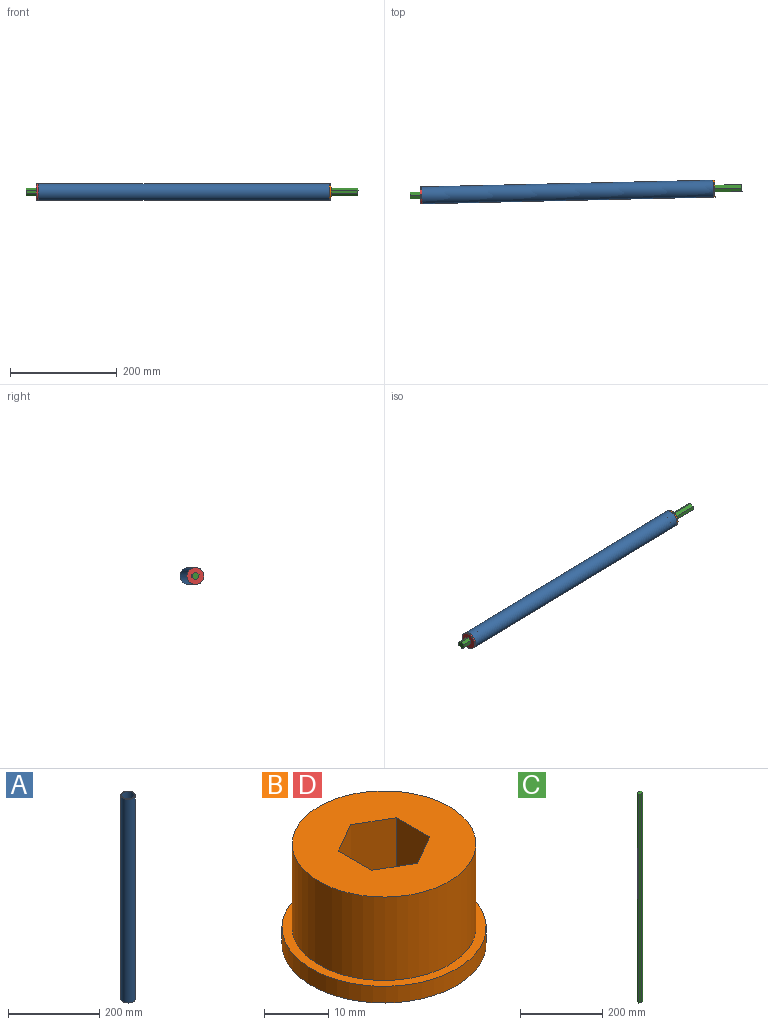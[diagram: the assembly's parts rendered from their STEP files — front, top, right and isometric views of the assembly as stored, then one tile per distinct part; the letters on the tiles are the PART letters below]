
ASSEMBLY  parts=4 mates=4
PART A: 4 faces, bbox 31.8x31.8x546.1 mm
  f0: cylinder r=14.29mm len=546.1mm, axis (0,0,-1), area 49023.9mm2, adj f2,f3
  f1: cylinder r=15.88mm len=546.1mm, axis (0,0,-1), area 54471.1mm2, adj f2,f3
  f2: plane 31.75x31.75mm, normal (0,0,1), area 150.4mm2, adj f0,f1
  f3: plane 31.75x31.75mm, normal (0,0,-1), area 150.4mm2, adj f0,f1
PART B: 11 faces, bbox 31.8x31.8x19.1 mm
  f0: cylinder r=15.88mm len=31.75mm, axis (0,0,-1), area 316.7mm2, adj f1,f2
  f1: plane 31.75x31.75mm, normal (0,0,1), area 150.4mm2, adj f0,f3
  f2: plane 31.75x31.75mm, normal (0,0,-1), area 652mm2, adj f0,f4,f5,f6,f7,f8,f9
  f3: cylinder r=14.29mm len=28.58mm, axis (0,0,-1), area 1425.1mm2, adj f1,f10
  f4: plane 19.05x6.35mm, normal (0.5,0.87,0), area 139.7mm2, adj f2,f5,f9,f10
  f5: plane 19.05x7.33mm, normal (1,0,0), area 139.7mm2, adj f2,f4,f6,f10
  f6: plane 19.05x6.35mm, normal (0.5,-0.87,0), area 139.7mm2, adj f2,f5,f7,f10
  f7: plane 19.05x6.35mm, normal (-0.5,-0.87,0), area 139.7mm2, adj f2,f6,f8,f10
  f8: plane 19.05x7.33mm, normal (-1,0,0), area 139.7mm2, adj f2,f7,f9,f10
  f9: plane 19.05x6.35mm, normal (-0.5,0.87,0), area 139.7mm2, adj f2,f4,f8,f10
  f10: plane 28.58x28.58mm, normal (0,0,1), area 501.6mm2, adj f3,f4,f5,f6,f7,f8,f9
PART C: 8 faces, bbox 13.7x14.5x622.3 mm
  f0: plane 622.3x7.25mm, normal (0.99,-0.15,0), area 4562.9mm2, adj f1,f5,f6,f7
  f1: plane 622.3x5.73mm, normal (0.62,0.78,0), area 4562.9mm2, adj f0,f2,f6,f7
  f2: plane 622.3x6.83mm, normal (-0.36,0.93,0), area 4562.9mm2, adj f1,f3,f6,f7
  f3: plane 622.3x7.25mm, normal (-0.99,0.15,0), area 4562.9mm2, adj f2,f4,f6,f7
  f4: plane 622.3x5.73mm, normal (-0.62,-0.78,0), area 4562.9mm2, adj f3,f5,f6,f7
  f5: plane 622.3x6.83mm, normal (0.36,-0.93,0), area 4562.9mm2, adj f0,f4,f6,f7
  f6: plane 14.5x13.66mm, normal (0,0,1), area 139.7mm2, adj f0,f1,f2,f3,f4,f5
  f7: plane 14.5x13.66mm, normal (0,0,-1), area 139.7mm2, adj f0,f1,f2,f3,f4,f5
PART D: same geometry as B
PLACE A rot(axis=(-0.59,0.57,-0.57),119.2deg) t=(58.77,-515.15,2.41)mm
PLACE B rot(axis=(0.59,-0.57,-0.57),119.2deg) t=(608.75,-539.36,-110.17)mm
PLACE C rot(axis=(-0.19,0.97,-0.17),91.7deg) t=(36.89,-530.39,-75.01)mm
PLACE D rot(axis=(-0.59,0.57,-0.57),119.2deg) t=(56.45,-552.06,-18.87)mm
MATE fastened C.f2 <-> B.f5  axis (-0.02,1,0) through (658.23,-481.41,-64.51)mm
MATE fastened D.f0 <-> A.f0  axis (1,0.02,0) through (58.46,-501.55,-64.52)mm
MATE fastened B.f0 <-> A.f0  axis (-1,-0.02,0) through (604.42,-488.99,-64.52)mm
MATE parallel B.f4 <-> C.f1  axis (0.01,-0.5,0.87) through (597.99,-485.96,-70.02)mm
